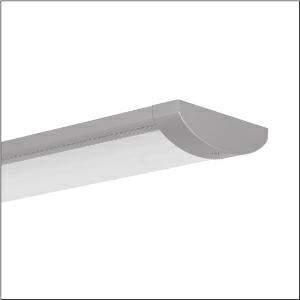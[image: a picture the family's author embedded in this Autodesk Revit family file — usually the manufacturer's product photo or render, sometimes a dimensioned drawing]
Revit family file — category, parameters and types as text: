
# Revit family: tv_20_5xa861d4n0x
name_source: partatom
category: Lighting Fixtures
units: mm (PartAtom-declared; Revit-internal decimal feet)

## family parameters
Cut with Voids When Loaded = No
Host = Face
Light Source = No
Part Type = Normal
Room Calculation Point = No
Round Connector Dimension = Use Diameter
Shared = No

## types (1)
- TV 20 (1 x LED 4000K / CRI = 80 (unbekannt), 5120 lm, 4000K)
    Apparent Load = 50 VA
    CIE Flux Codes = 48 78 95 99 100
    Color Rendering = 80
    Color Temperature = 4000K
    Default Elevation = 1800 mm
    Description = TV 20, vandal-proof luminaire, primary light control with specular reflector, of aluminium, matt, primary optical cover: enclosure, of PC, frosted, light emission: direct distribution, primary light characteristic: symmetric, installation type: surface-mounted, LED, rated luminous flux: 5.120lm, luminous efficacy: 102lm/W, light colour: 840, colour temperature: 4000K, control gear: DALI, mains connection: 230V, AC, 50Hz, rated input power: 50W, luminaire housing, of aluminium, coated, SITECO metallic grey (DB 702S), with wall and ceiling fixing element, length: 1.561mm, width: 260mm, height: 70mm, mounting height: 2.5..4.0m, protection rating (complete): IP65, insulation class (complete): insulation class I (protective earthing), certification: CE, protection symbol: F, impact resistance: 2x IK10, standard: EN 60598, packaging unit: 1 piece
    Height = 70 mm
    Lamp = 1 x LED 4000K / CRI >= 80 (unbekannt)
    Lamp Light Flux = 5120 lm
    Lamp count = 1
    Length = 1561 mm
    Luminous efficacy = 102 lm/W
    Manufacturer = Siteco
    ModVariant = No
    Model = 5XA861D4N0X
    Mounting Place = Ceiling
    Mounting Type = Surface mounted
    Number of Poles = 1
    OnlyDefault = Yes
    Power Factor = 1
    Product Name = TV 20
    Product group = vandal-proof luminaire
    ProductGroupID = 310
    Protection Class = Protection class I
    Protection Degree = IP 65
    RLX_Detail_Level = 1
    RLX_Emergency_Light_Flux = 0 lm
    RLX_Emergency_Type = 0
    RLX_Emergency_Type_DB = No
    RlxData = <blob elided: 25309 chars, md5=31496626>
    Socket = socket
    Standby Power = 0 W
    System Light Flux = 5120 lm
    System Power = 50 W
    Type Comments = Product without accessories
    Type Image = l_1004809.jpg
    URL = http://relux.com
    VarID = ---
    Voltage = 0 V
    Weight = 0.00 kg
    Width = 260 mm

## geometry (parser evidence)
native form markers: Blend x4, Sweep x11
no freeform markers — native parametric forms only
